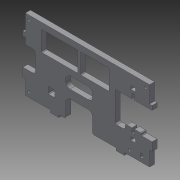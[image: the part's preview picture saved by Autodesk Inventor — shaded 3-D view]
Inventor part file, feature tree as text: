
AUTODESK INVENTOR PART (.ipt)
format: ipt  version: 2015 (Build 190159000, 159)  size: 330,240 bytes
history: native  units: mm
features: extrude x7, sketch x7, fillet x6
ambient origin geometry x8: Origin, YZ Plane, XZ Plane, XY Plane, X Axis, Y Axis, Z Axis, Center Point
bodies: Solid1 (feature_tree)
feature tree (20):
  extrude  "Extrusion1"  Depth=3.0mm
  sketch  "Sketch3"  dims[d14=6.0mm d15=0.0mm d28=20.0mm]
  sketch  "Sketch10"  dims[d41=10.0mm d42=3.0mm d44=30.0mm d84=3.0mm d88=3.0mm]
  extrude  "Extrusion10"  Depth=20.0mm
  extrude  "Extrusion6"  Depth=48.0mm
  extrude  "Extrusion8"  Depth=3.0mm
  fillet  "Fillet10"  Radius=30.0mm
  fillet  "Fillet11"  Radius=3.0mm
  fillet  "Fillet12"  Radius=3.0mm
  extrude  "Extrusion11"  Depth=3.0mm
  fillet  "Fillet13"  Radius=139.0mm
  fillet  "Fillet14"  Radius=3.0mm
  extrude  "Extrusion12"  Depth=10.0mm TaperAngle=0.0deg
  extrude  "Extrusion13"  Depth=10.0mm TaperAngle=0.0deg
  fillet  "Fillet16"  Radius=2.0mm
  sketch  "Sketch1"  dims[d0=85.0mm d6=3.0mm]
  sketch  "Sketch7"  dims[d33=6.0mm d34=38.0mm d35=48.0mm]
  sketch  "Sketch11"  dims[d89=74.0mm d90=3.0mm d91=139.0mm d92=3.0mm]
  sketch  "Sketch12"  dims[d93=19.0mm d94=10.0mm d95=0.0mm]
  sketch  "Sketch13"  dims[d106=10.0mm d118=10.0mm d119=0.0mm d129=2.0mm d130=32.0mm d131=5.0mm d133=5.0mm d134=5.5mm d144=33.0mm d145=10.0mm d146=5.0mm d147=5.0mm d149=32.0mm d150=5.0mm d158=12.5mm d159=41.0mm d160=18.0mm d161=6.0mm d162=3.0mm d163=10.0mm d164=10.0mm d165=8.0mm d167=5.8mm d168=4.0mm d170=3.5mm d171=10.0mm d172=0.0mm d173=48.0mm d174=2.0mm d175=1.0mm d176=8.0mm d177=8.0mm d178=5.0mm d179=10.0mm d180=0.0mm d181=1.0mm d182=12.0mm d183=3.0mm d184=20.0mm d187=8.0mm d190=3.0mm d191=5.0mm d192=3.0mm d196=10.0mm d197=0.0mm d201=7.0mm d203=7.0mm d204=7.0mm d205=7.0mm d206=3.0mm d207=2.0mm d208=2.0mm d212=2.0mm d218=3.0mm d238=3.0mm d239=3.0mm d247=7.0mm d251=2.0mm d255=10.0mm d256=0.0mm d262=1.0mm d266=7.0mm d267=7.0mm d268=3.0mm d269=1.0mm]
